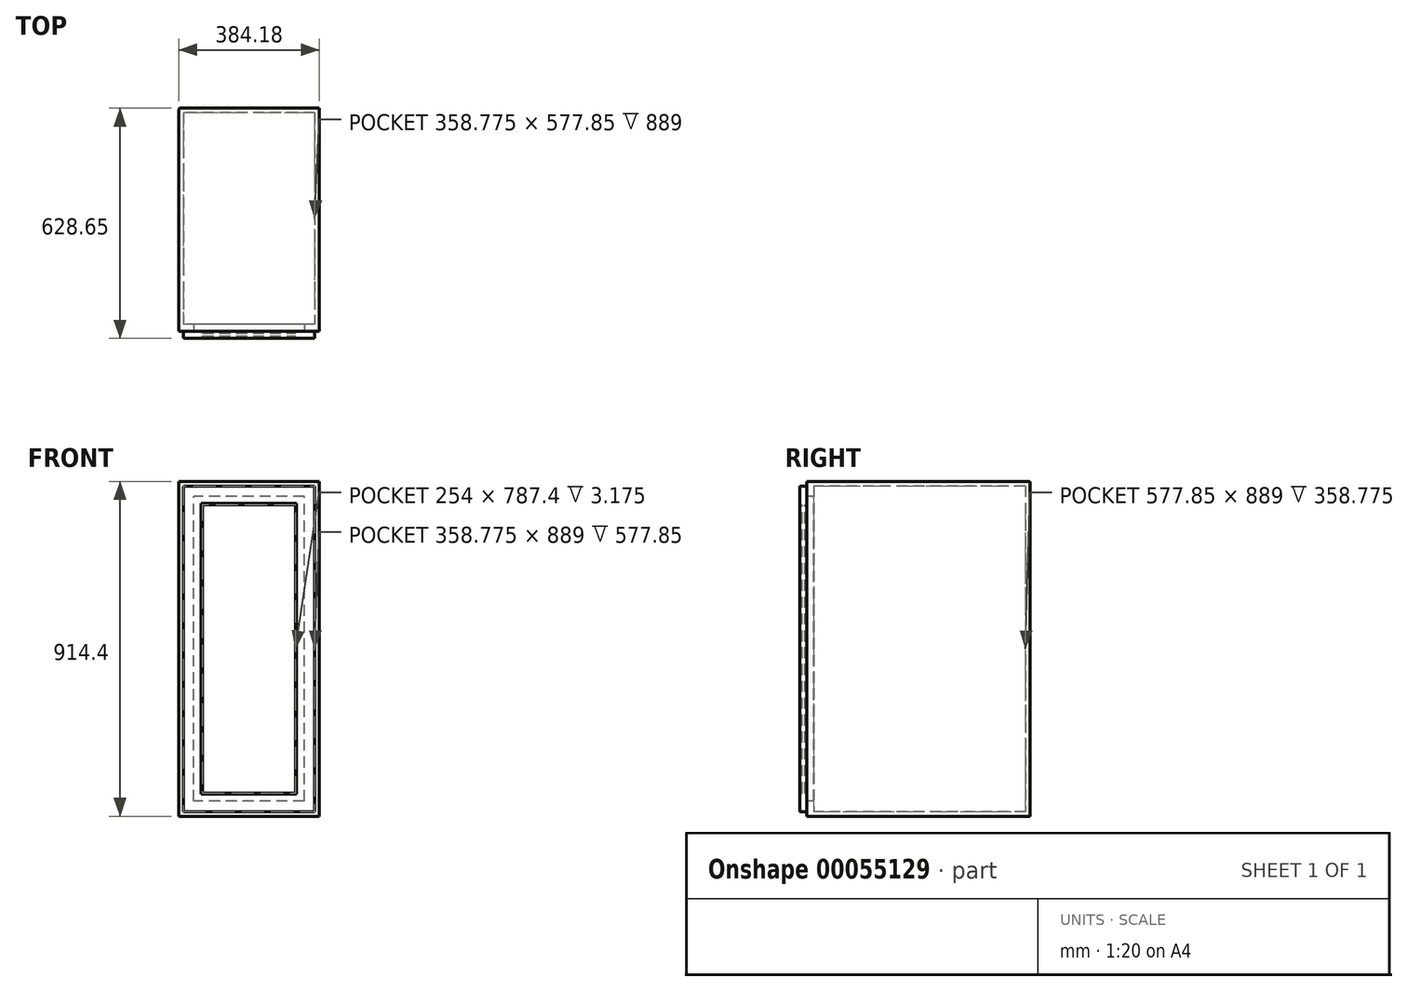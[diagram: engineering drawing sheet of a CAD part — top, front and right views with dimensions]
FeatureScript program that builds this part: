
annotation { "Feature Type Name" : "Feature", "Feature Type Description" : "" }
export const myFeature = defineFeature(function(context is Context, id is Id, definition is map)
    precondition{}
    {
        {
            var Q0;
            Q0=qCreatedBy(makeId("Top.planeOp"),FACE);
            var sketch = newSketch(context, id + "F0", { "sketchPlane" : qUnion([Q0])});
            skLineSegment(sketch, "E0.rect.bottom", {"start": v(192.09, 304.8) * mm, "end": v(-192.09, 304.8) * mm});
            skLineSegment(sketch, "E0.rect.top", {"start": v(192.09, -304.8) * mm, "end": v(-192.09, -304.8) * mm});
            skLineSegment(sketch, "E0.rect.left", {"start": v(192.09, 304.8) * mm, "end": v(192.09, -304.8) * mm});
            skLineSegment(sketch, "E0.rect.right", {"start": v(-192.09, 304.8) * mm, "end": v(-192.09, -304.8) * mm});
            skPoint(sketch, "E0.rect.middle", {"position": v(0, 0) * mm});
            skSolve(sketch);
        }
        {
            var Q0;
            Q0 = qSketchRegion(id + "F0", true);
            extrude(context, id + "F1", {"entities" : qUnion([Q0]), "depth" : 914.4 * mm});
        }
        {
            var Q0;
            Q0=makeQuery(id+"F1.opExtrude","SWEPT_FACE",FACE,{"disambiguationData":[OSD([sQuery(id+"F0.wireOp",EDGE,"E0.rect.top")])]});
            shell(context, id + "F2", {"entities" : qUnion([Q0]), "thickness" : 12.7 * mm});
        }
        {
            var Q0;
            Q0=makeQuery(id+"F1.opExtrude","SWEPT_FACE",FACE,{"disambiguationData":[OSD([sQuery(id+"F0.wireOp",EDGE,"E0.rect.top")])]});
            var sketch = newSketch(context, id + "F3", { "sketchPlane" : qUnion([Q0])});
            skLineSegment(sketch, "E1", {"start": v(192.09, 914.4) * mm, "end": v(-192.09, 0) * mm, "construction": true});
            skLineSegment(sketch, "E2.rect.bottom", {"start": v(150.81, 41.28) * mm, "end": v(-150.81, 41.28) * mm});
            skLineSegment(sketch, "E2.rect.top", {"start": v(150.81, 873.12) * mm, "end": v(-150.81, 873.12) * mm});
            skLineSegment(sketch, "E2.rect.left", {"start": v(150.81, 41.28) * mm, "end": v(150.81, 873.13) * mm});
            skLineSegment(sketch, "E2.rect.right", {"start": v(-150.81, 41.28) * mm, "end": v(-150.81, 873.13) * mm});
            skPoint(sketch, "E2.rect.middle", {"position": v(0, 457.2) * mm});
            skLineSegment(sketch, "E3.rect.bottom", {"start": v(184.15, 6.35) * mm, "end": v(-184.15, 6.35) * mm});
            skLineSegment(sketch, "E3.rect.top", {"start": v(184.15, 908.05) * mm, "end": v(-184.15, 908.05) * mm});
            skLineSegment(sketch, "E3.rect.left", {"start": v(184.15, 6.35) * mm, "end": v(184.15, 908.05) * mm});
            skLineSegment(sketch, "E3.rect.right", {"start": v(-184.15, 6.35) * mm, "end": v(-184.15, 908.05) * mm});
            skLineSegment(sketch, "E4.rect.bottom", {"start": v(127, 63.5) * mm, "end": v(-127, 63.5) * mm});
            skLineSegment(sketch, "E4.rect.top", {"start": v(127, 850.9) * mm, "end": v(-127, 850.9) * mm});
            skLineSegment(sketch, "E4.rect.left", {"start": v(127, 63.5) * mm, "end": v(127, 850.9) * mm});
            skLineSegment(sketch, "E4.rect.right", {"start": v(-127, 63.5) * mm, "end": v(-127, 850.9) * mm});
            skSolve(sketch);
        }
        {
            var Q0;
            Q0=makeQuery(id+"F3.imprint","IMPRINT",FACE,{"disambiguationData":[TD([[makeQuery(id+"F3.imprint","IMPRINT",EDGE,{"derivedFrom":sQuery(id+"F3.wireOp",EDGE,"E2.rect.bottom")}),1.0]])]});
            var Q1;
            {var subQ0=sQuery(id+"F0.wireOp",EDGE,"E0.rect.top");var subQ3=makeQuery(id+"F1.opExtrude","CAP_EDGE",EDGE,{"disambiguationData":[OSD([subQ0])],"isStart":true});Q1=makeQuery(id+"F3.imprint","IMPRINT",FACE,{"disambiguationData":[TD([[makeQuery(id+"F3.imprint","IMPRINT",EDGE,{"derivedFrom":subQ3}),-1.0]])]});}
            extrude(context, id + "F4", {"entities" : qUnion([Q0, Q1]), "operationType" : NewBodyOperationType.ADD, "oppositeDirection" : true, "depth" : 19.05 * mm});
        }
        {
            var Q0;
            Q0=makeQuery(id+"F3.imprint","IMPRINT",FACE,{"disambiguationData":[TD([[makeQuery(id+"F3.imprint","IMPRINT",EDGE,{"derivedFrom":sQuery(id+"F3.wireOp",EDGE,"E2.rect.bottom")}),1.0]])]});
            var Q1;
            Q1=makeQuery(id+"F3.imprint","IMPRINT",FACE,{"disambiguationData":[TD([[makeQuery(id+"F3.imprint","IMPRINT",EDGE,{"derivedFrom":sQuery(id+"F3.wireOp",EDGE,"E2.rect.bottom")}),-1.0]])]});
            extrude(context, id + "F5", {"entities" : qUnion([Q0, Q1]), "operationType" : NewBodyOperationType.ADD, "depth" : 19.05 * mm});
        }
        {
            var Q0;
            Q0=makeQuery(id+"F5.opExtrude","SWEPT_FACE",FACE,{"disambiguationData":[OSD([sQuery(id+"F3.wireOp",EDGE,"E4.rect.top")])]});
            var sketch = newSketch(context, id + "F6", { "sketchPlane" : qUnion([Q0])});
            skLineSegment(sketch, "E5.bottom", {"start": v(-127, 309.56) * mm, "end": v(127, 309.56) * mm});
            skLineSegment(sketch, "E5.top", {"start": v(-127, 317.5) * mm, "end": v(127, 317.5) * mm});
            skLineSegment(sketch, "E5.left", {"start": v(-127, 309.56) * mm, "end": v(-127, 317.5) * mm});
            skLineSegment(sketch, "E5.right", {"start": v(127, 309.56) * mm, "end": v(127, 317.5) * mm});
            skSolve(sketch);
        }
        {
            var Q0;
            Q0 = qSketchRegion(id + "F6", true);
            extrude(context, id + "F7", {"entities" : qUnion([Q0]), "operationType" : NewBodyOperationType.ADD, "endBound" : BoundingType.UP_TO_NEXT, "depth" : 25.4 * mm});
        }
        {
            var Q0;
            Q0=makeQuery(id+"F5.opExtrude","CAP_EDGE",EDGE,{"disambiguationData":[OSD([sQuery(id+"F3.wireOp",EDGE,"E4.rect.bottom")])],"isStart":false});
            var Q1;
            Q1=makeQuery(id+"F5.opExtrude","CAP_EDGE",EDGE,{"disambiguationData":[OSD([sQuery(id+"F3.wireOp",EDGE,"E4.rect.right")])],"isStart":false});
            var Q2;
            Q2=makeQuery(id+"F5.opExtrude","CAP_EDGE",EDGE,{"disambiguationData":[OSD([sQuery(id+"F3.wireOp",EDGE,"E4.rect.left")])],"isStart":false});
            var Q3;
            Q3=makeQuery(id+"F5.opExtrude","CAP_EDGE",EDGE,{"disambiguationData":[OSD([sQuery(id+"F3.wireOp",EDGE,"E4.rect.top")])],"isStart":false});
            var Q4;
            Q4=makeQuery(id+"F1.opExtrude","SWEPT_EDGE",EDGE,{"disambiguationData":[OSD([sQuery(id+"F0.wireOp",EDGE,"E0.rect.bottom"),sQuery(id+"F0.wireOp",EDGE,"E0.rect.right")])]});
            chamfer(context, id + "F8", {"entities" : qUnion([Q0, Q1, Q2, Q3, Q4]), "width" : 3.17 * mm, "tangentPropagation" : true});
        }
    });
